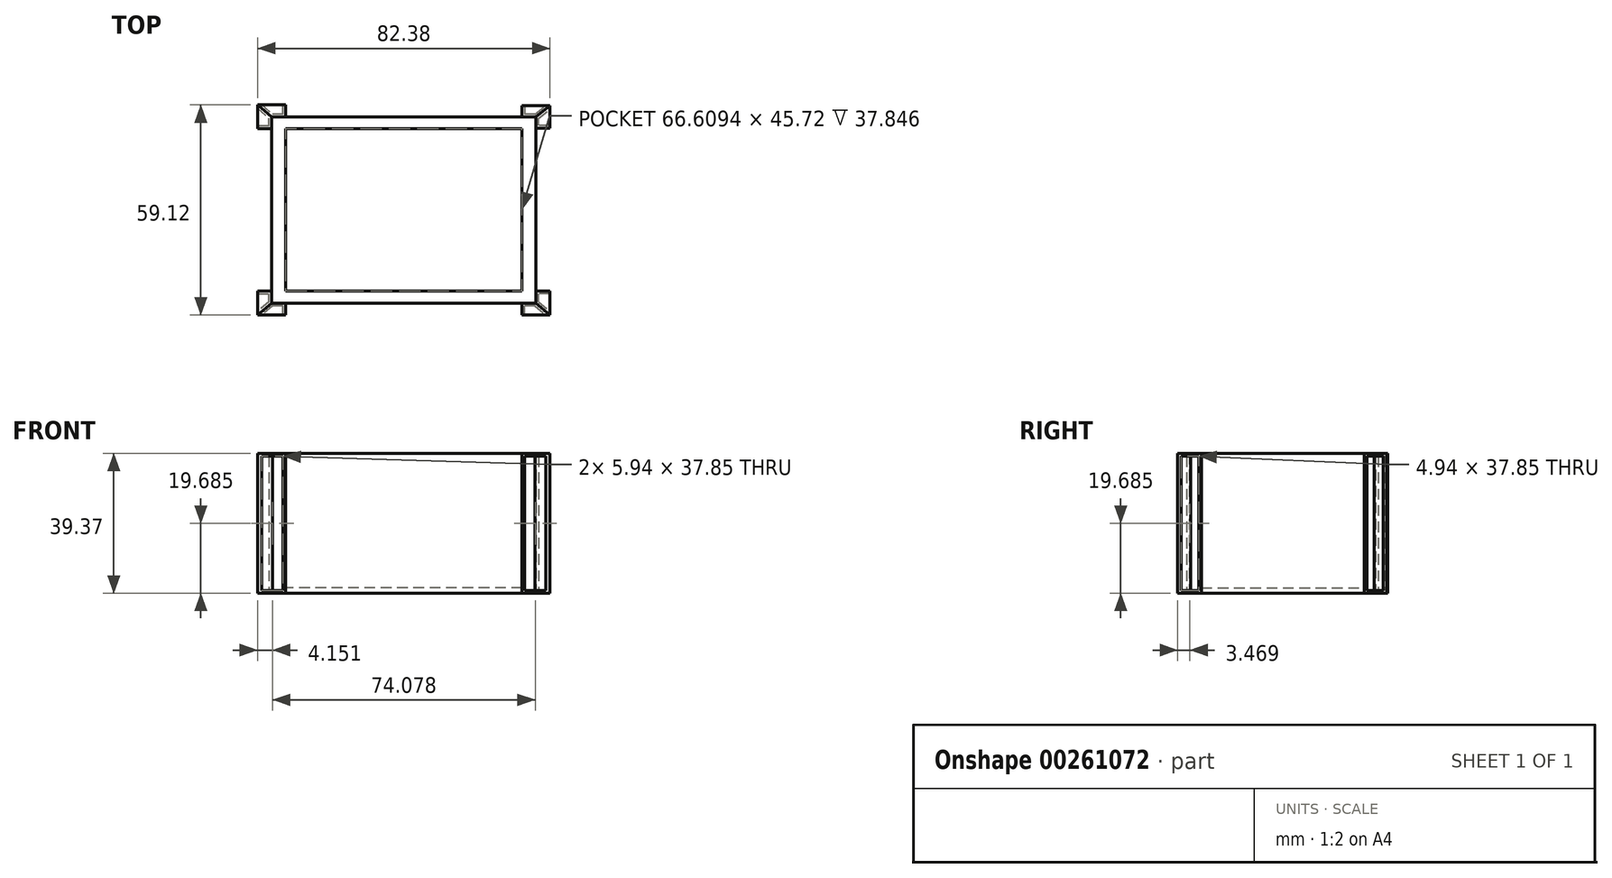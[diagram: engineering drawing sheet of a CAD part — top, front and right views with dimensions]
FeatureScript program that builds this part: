
annotation { "Feature Type Name" : "Feature", "Feature Type Description" : "" }
export const myFeature = defineFeature(function(context is Context, id is Id, definition is map)
    precondition{}
    {
        {
            var Q0;
            Q0=qCreatedBy(makeId("Top.planeOp"),FACE);
            var sketch = newSketch(context, id + "F0", { "sketchPlane" : qUnion([Q0])});
            skPoint(sketch, "E0.middle", {"position": v(0, 0) * mm});
            skLineSegment(sketch, "E1.bottom", {"start": v(33.3, -22.86) * mm, "end": v(-33.3, -22.86) * mm});
            skLineSegment(sketch, "E1.top", {"start": v(33.3, 22.86) * mm, "end": v(-33.3, 22.86) * mm});
            skLineSegment(sketch, "E1.left", {"start": v(33.3, -22.86) * mm, "end": v(33.3, 22.86) * mm});
            skLineSegment(sketch, "E1.right", {"start": v(-33.3, -22.86) * mm, "end": v(-33.3, 22.86) * mm});
            skPoint(sketch, "E2.middle", {"position": v(0, -22.86) * mm});
            skPoint(sketch, "E2.cornerSnap0", {"position": v(0, -22.86) * mm});
            skLineSegment(sketch, "E3.bottom", {"start": v(37.25, -26.21) * mm, "end": v(-37.25, -26.21) * mm});
            skLineSegment(sketch, "E3.top", {"start": v(37.25, 26.21) * mm, "end": v(-37.25, 26.21) * mm});
            skLineSegment(sketch, "E3.left", {"start": v(37.25, -26.21) * mm, "end": v(37.25, 26.21) * mm});
            skLineSegment(sketch, "E3.right", {"start": v(-37.25, -26.21) * mm, "end": v(-37.25, 26.21) * mm});
            skLineSegment(sketch, "E4.bottom", {"start": v(-33.3, 22.86) * mm, "end": v(-41.19, 22.86) * mm});
            skLineSegment(sketch, "E4.top", {"start": v(-33.3, 29.56) * mm, "end": v(-41.19, 29.56) * mm});
            skLineSegment(sketch, "E4.left", {"start": v(-33.3, 22.86) * mm, "end": v(-33.3, 29.56) * mm});
            skLineSegment(sketch, "E4.right", {"start": v(-41.19, 22.86) * mm, "end": v(-41.19, 29.56) * mm});
            skPoint(sketch, "E4.middle", {"position": v(-37.25, 26.21) * mm});
            skLineSegment(sketch, "E5.bottom", {"start": v(41.19, 29.36) * mm, "end": v(33.3, 29.36) * mm});
            skLineSegment(sketch, "E5.top", {"start": v(41.19, 23.06) * mm, "end": v(33.3, 23.06) * mm});
            skLineSegment(sketch, "E5.left", {"start": v(41.19, 29.36) * mm, "end": v(41.19, 23.06) * mm});
            skLineSegment(sketch, "E5.right", {"start": v(33.3, 29.36) * mm, "end": v(33.3, 23.06) * mm});
            skPoint(sketch, "E5.middle", {"position": v(37.25, 26.21) * mm});
            skLineSegment(sketch, "E6.bottom", {"start": v(41.19, -29.56) * mm, "end": v(33.3, -29.56) * mm});
            skLineSegment(sketch, "E6.top", {"start": v(41.19, -22.86) * mm, "end": v(33.3, -22.86) * mm});
            skLineSegment(sketch, "E6.left", {"start": v(41.19, -29.56) * mm, "end": v(41.19, -22.86) * mm});
            skLineSegment(sketch, "E6.right", {"start": v(33.3, -29.56) * mm, "end": v(33.3, -22.86) * mm});
            skPoint(sketch, "E6.middle", {"position": v(37.25, -26.21) * mm});
            skPoint(sketch, "E6.cornerSnap0", {"position": v(41.19, 26.21) * mm});
            skLineSegment(sketch, "E7.bottom", {"start": v(-41.19, -29.56) * mm, "end": v(-33.3, -29.56) * mm});
            skLineSegment(sketch, "E7.top", {"start": v(-41.19, -22.86) * mm, "end": v(-33.3, -22.86) * mm});
            skLineSegment(sketch, "E7.left", {"start": v(-41.19, -29.56) * mm, "end": v(-41.19, -22.86) * mm});
            skLineSegment(sketch, "E7.right", {"start": v(-33.3, -29.56) * mm, "end": v(-33.3, -22.86) * mm});
            skPoint(sketch, "E7.middle", {"position": v(-37.25, -26.21) * mm});
            skPoint(sketch, "E7.cornerSnap0", {"position": v(37.25, -29.56) * mm});
            skLineSegment(sketch, "E8", {"start": v(-41.19, 29.56) * mm, "end": v(-37.25, 26.21) * mm});
            skLineSegment(sketch, "E9", {"start": v(37.25, 26.21) * mm, "end": v(41.19, 29.36) * mm});
            skLineSegment(sketch, "E10", {"start": v(37.25, -26.21) * mm, "end": v(41.19, -29.56) * mm});
            skLineSegment(sketch, "E11", {"start": v(-37.25, -26.21) * mm, "end": v(-41.19, -29.56) * mm});
            skSolve(sketch);
        }
        {
            var Q0;
            Q0=makeQuery(id+"F0.imprint","IMPRINT",FACE,{"disambiguationData":[TD([[makeQuery(id+"F0.imprint","IMPRINT",EDGE,{"derivedFrom":sQuery(id+"F0.wireOp",EDGE,"E1.bottom")}),-1.0]])]});
            extrude(context, id + "F1", {"entities" : qUnion([Q0]), "depth" : 1.52 * mm});
        }
        {
            var Q0;
            {var subQ0=sQuery(id+"F0.wireOp",EDGE,"E1.bottom");Q0=makeQuery(id+"F0.imprint","IMPRINT",FACE,{"disambiguationData":[TD([[makeQuery(id+"F0.imprint","IMPRINT",EDGE,{"derivedFrom":subQ0}),1.0]])]});}
            var Q1;
            {var subQ0=sQuery(id+"F0.wireOp",EDGE,"E1.right");Q1=makeQuery(id+"F0.imprint","IMPRINT",FACE,{"disambiguationData":[TD([[makeQuery(id+"F0.imprint","IMPRINT",EDGE,{"derivedFrom":subQ0}),1.0]])]});}
            var Q2;
            {var subQ3=sQuery(id+"F0.wireOp",EDGE,"E5.right");var subQ5=sQuery(id+"F0.wireOp",EDGE,"E5.top");var subQ7=makeQuery(id+"F0.imprint","INTERSECT",VERTEX,{"derivedFrom":[subQ5,subQ3]});Q2=makeQuery(id+"F0.imprint","IMPRINT",FACE,{"disambiguationData":[TD([[makeQuery(id+"F0.imprint","IMPRINT",EDGE,{"disambiguationData":[TD([[subQ7,1.0]])],"derivedFrom":subQ5}),-1.0]])]});}
            var Q3;
            {var subQ10=sQuery(id+"F0.wireOp",EDGE,"E1.top");Q3=makeQuery(id+"F0.imprint","IMPRINT",FACE,{"disambiguationData":[TD([[makeQuery(id+"F0.imprint","IMPRINT",EDGE,{"derivedFrom":subQ10}),-1.0]])]});}
            var Q4;
            {var subQ1=sQuery(id+"F0.wireOp",EDGE,"E3.bottom");var subQ3=sQuery(id+"F0.wireOp",EDGE,"E6.right");var subQ4=makeQuery(id+"F0.imprint","INTERSECT",VERTEX,{"derivedFrom":[subQ1,subQ3]});Q4=makeQuery(id+"F0.imprint","IMPRINT",FACE,{"disambiguationData":[TD([[makeQuery(id+"F0.imprint","IMPRINT",EDGE,{"disambiguationData":[TD([[subQ4,1.0]])],"derivedFrom":subQ1}),-1.0]])]});}
            var Q5;
            {var subQ1=sQuery(id+"F0.wireOp",EDGE,"E3.bottom");var subQ3=sQuery(id+"F0.wireOp",EDGE,"E7.right");var subQ4=makeQuery(id+"F0.imprint","INTERSECT",VERTEX,{"derivedFrom":[subQ1,subQ3]});Q5=makeQuery(id+"F0.imprint","IMPRINT",FACE,{"disambiguationData":[TD([[makeQuery(id+"F0.imprint","IMPRINT",EDGE,{"disambiguationData":[TD([[subQ4,-1.0]])],"derivedFrom":subQ1}),-1.0]])]});}
            var Q6;
            {var subQ1=sQuery(id+"F0.wireOp",EDGE,"E3.top");var subQ3=sQuery(id+"F0.wireOp",EDGE,"E4.left");var subQ4=makeQuery(id+"F0.imprint","INTERSECT",VERTEX,{"derivedFrom":[subQ1,subQ3]});Q6=makeQuery(id+"F0.imprint","IMPRINT",FACE,{"disambiguationData":[TD([[makeQuery(id+"F0.imprint","IMPRINT",EDGE,{"disambiguationData":[TD([[subQ4,-1.0]])],"derivedFrom":subQ1}),1.0]])]});}
            extrude(context, id + "F2", {"entities" : qUnion([Q0, Q1, Q2, Q3, Q4, Q5, Q6]), "operationType" : NewBodyOperationType.ADD, "depth" : 39.37 * mm});
        }
        {
            var Q0;
            {var subQ4=sQuery(id+"F0.wireOp",EDGE,"E4.right");Q0=makeQuery(id+"F0.imprint","IMPRINT",FACE,{"disambiguationData":[TD([[makeQuery(id+"F0.imprint","IMPRINT",EDGE,{"derivedFrom":subQ4}),-1.0]])]});}
            var Q1;
            {var subQ4=sQuery(id+"F0.wireOp",EDGE,"E7.bottom");Q1=makeQuery(id+"F0.imprint","IMPRINT",FACE,{"disambiguationData":[TD([[makeQuery(id+"F0.imprint","IMPRINT",EDGE,{"derivedFrom":subQ4}),1.0]])]});}
            var Q2;
            {var subQ4=sQuery(id+"F0.wireOp",EDGE,"E6.left");Q2=makeQuery(id+"F0.imprint","IMPRINT",FACE,{"disambiguationData":[TD([[makeQuery(id+"F0.imprint","IMPRINT",EDGE,{"derivedFrom":subQ4}),1.0]])]});}
            var Q3;
            {var subQ4=sQuery(id+"F0.wireOp",EDGE,"E5.left");Q3=makeQuery(id+"F0.imprint","IMPRINT",FACE,{"disambiguationData":[TD([[makeQuery(id+"F0.imprint","IMPRINT",EDGE,{"derivedFrom":subQ4}),-1.0]])]});}
            extrude(context, id + "F3", {"entities" : qUnion([Q0, Q1, Q2, Q3]), "depth" : 39.37 * mm});
        }
        {
            var Q0;
            {var subQ4=sQuery(id+"F0.wireOp",EDGE,"E4.top");Q0=makeQuery(id+"F0.imprint","IMPRINT",FACE,{"disambiguationData":[TD([[makeQuery(id+"F0.imprint","IMPRINT",EDGE,{"derivedFrom":subQ4}),1.0]])]});}
            var Q1;
            {var subQ4=sQuery(id+"F0.wireOp",EDGE,"E7.left");Q1=makeQuery(id+"F0.imprint","IMPRINT",FACE,{"disambiguationData":[TD([[makeQuery(id+"F0.imprint","IMPRINT",EDGE,{"derivedFrom":subQ4}),-1.0]])]});}
            var Q2;
            {var subQ4=sQuery(id+"F0.wireOp",EDGE,"E6.bottom");Q2=makeQuery(id+"F0.imprint","IMPRINT",FACE,{"disambiguationData":[TD([[makeQuery(id+"F0.imprint","IMPRINT",EDGE,{"derivedFrom":subQ4}),-1.0]])]});}
            var Q3;
            {var subQ4=sQuery(id+"F0.wireOp",EDGE,"E5.bottom");Q3=makeQuery(id+"F0.imprint","IMPRINT",FACE,{"disambiguationData":[TD([[makeQuery(id+"F0.imprint","IMPRINT",EDGE,{"derivedFrom":subQ4}),1.0]])]});}
            extrude(context, id + "F4", {"entities" : qUnion([Q0, Q1, Q2, Q3]), "depth" : 39.37 * mm});
        }
        {
            var Q0;
            Q0=makeQuery(id+"F3.opExtrude","SWEPT_FACE",FACE,{"disambiguationData":[OSD([sQuery(id+"F0.wireOp",EDGE,"E7.bottom")])]});
            var Q1;
            Q1=makeQuery(id+"F4.opExtrude","SWEPT_FACE",FACE,{"disambiguationData":[OSD([sQuery(id+"F0.wireOp",EDGE,"E6.bottom")])]});
            var Q2;
            Q2=makeQuery(id+"F3.opExtrude","SWEPT_FACE",FACE,{"disambiguationData":[OSD([sQuery(id+"F0.wireOp",EDGE,"E6.left")])]});
            var Q3;
            Q3=makeQuery(id+"F3.opExtrude","SWEPT_FACE",FACE,{"disambiguationData":[OSD([sQuery(id+"F0.wireOp",EDGE,"E5.left")])]});
            var Q4;
            Q4=makeQuery(id+"F4.opExtrude","SWEPT_FACE",FACE,{"disambiguationData":[OSD([sQuery(id+"F0.wireOp",EDGE,"E5.bottom")])]});
            var Q5;
            Q5=makeQuery(id+"F4.opExtrude","SWEPT_FACE",FACE,{"disambiguationData":[OSD([sQuery(id+"F0.wireOp",EDGE,"E4.top")])]});
            var Q6;
            Q6=makeQuery(id+"F4.opExtrude","SWEPT_FACE",FACE,{"disambiguationData":[OSD([sQuery(id+"F0.wireOp",EDGE,"E7.left")])]});
            var Q7;
            Q7=makeQuery(id+"F3.opExtrude","SWEPT_FACE",FACE,{"disambiguationData":[OSD([sQuery(id+"F0.wireOp",EDGE,"E4.right")])]});
            shell(context, id + "F5", {"entities" : qUnion([Q0, Q1, Q2, Q3, Q4, Q5, Q6, Q7]), "thickness" : 0.76 * mm});
        }
    });
